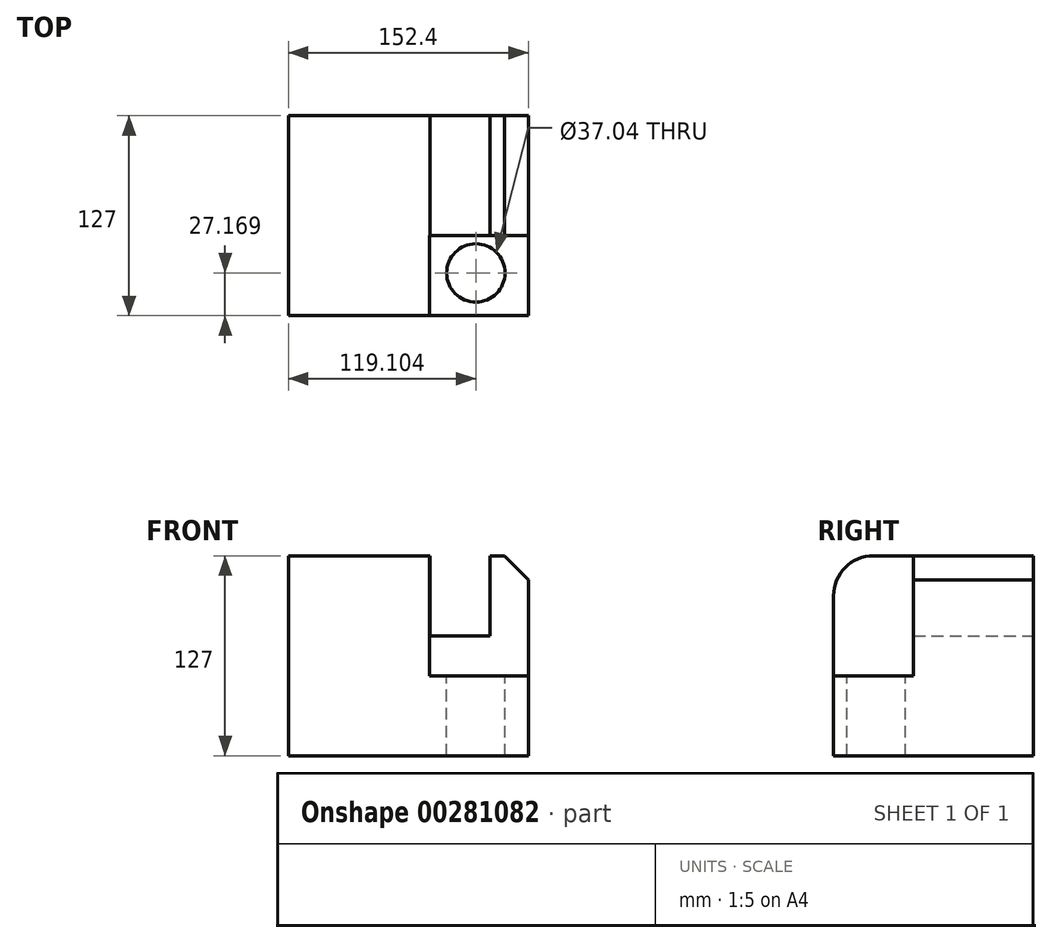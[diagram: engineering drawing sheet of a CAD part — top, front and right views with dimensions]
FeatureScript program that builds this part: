
annotation { "Feature Type Name" : "Feature", "Feature Type Description" : "" }
export const myFeature = defineFeature(function(context is Context, id is Id, definition is map)
    precondition{}
    {
        {
            var Q0;
            Q0=qCreatedBy(makeId("Front.planeOp"),FACE);
            var sketch = newSketch(context, id + "F0", { "sketchPlane" : qUnion([Q0])});
            skLineSegment(sketch, "E0.bottom", {"start": v(-72.36, 54.29) * mm, "end": v(80.04, 54.29) * mm});
            skLineSegment(sketch, "E0.top", {"start": v(-72.36, -72.71) * mm, "end": v(80.04, -72.71) * mm});
            skLineSegment(sketch, "E0.left", {"start": v(-72.36, 54.29) * mm, "end": v(-72.36, -72.71) * mm});
            skLineSegment(sketch, "E0.right", {"start": v(80.04, 54.29) * mm, "end": v(80.04, -72.71) * mm});
            skSolve(sketch);
        }
        {
            var Q0;
            Q0=makeQuery(id+"F0.imprint","IMPRINT",FACE,{"disambiguationData":[TD([[makeQuery(id+"F0.imprint","IMPRINT",EDGE,{"derivedFrom":sQuery(id+"F0.wireOp",EDGE,"E0.bottom")}),-1.0]])]});
            extrude(context, id + "F1", {"entities" : qUnion([Q0]), "depth" : 127 * mm});
        }
        {
            var Q0;
            Q0=makeQuery(id+"F1.opExtrude","SWEPT_FACE",FACE,{"disambiguationData":[OSD([sQuery(id+"F0.wireOp",EDGE,"E0.bottom")])]});
            var sketch = newSketch(context, id + "F2", { "sketchPlane" : qUnion([Q0])});
            skLineSegment(sketch, "E1", {"start": v(80.04, -127) * mm, "end": v(17.28, -127) * mm});
            skLineSegment(sketch, "E2", {"start": v(17.28, -127) * mm, "end": v(17.28, -76.2) * mm});
            skLineSegment(sketch, "E3", {"start": v(17.28, -76.2) * mm, "end": v(80.04, -76.2) * mm});
            skLineSegment(sketch, "E4", {"start": v(80.04, -76.2) * mm, "end": v(80.04, -127) * mm});
            skSolve(sketch);
        }
        {
            var Q0;
            Q0=makeQuery(id+"F2.imprint","IMPRINT",FACE,{"disambiguationData":[TD([[makeQuery(id+"F2.imprint","IMPRINT",EDGE,{"derivedFrom":sQuery(id+"F2.wireOp",EDGE,"E1")}),1.0]])]});
            extrude(context, id + "F3", {"entities" : qUnion([Q0]), "operationType" : NewBodyOperationType.REMOVE, "oppositeDirection" : true, "depth" : 76.2 * mm});
        }
        {
            var Q0;
            Q0=makeQuery(id+"F3.boolean.opBoolean","COPY",FACE,{"derivedFrom":makeQuery(id+"F3.opExtrude","CAP_FACE",FACE,{"disambiguationData":[OSD([sQuery(id+"F2.wireOp",EDGE,"E1"),sQuery(id+"F2.wireOp",EDGE,"E2"),sQuery(id+"F2.wireOp",EDGE,"E3"),sQuery(id+"F2.wireOp",EDGE,"E4")])],"isStart":false})});
            var sketch = newSketch(context, id + "F4", { "sketchPlane" : qUnion([Q0])});
            skCircle(sketch, "E5", {"center": v(46.74, -99.83) * mm, "radius": 18.52 * mm});
            skSolve(sketch);
        }
        {
            var Q0;
            Q0=makeQuery(id+"F4.imprint","IMPRINT",FACE,{"disambiguationData":[TD([[makeQuery(id+"F4.imprint","IMPRINT",EDGE,{"derivedFrom":sQuery(id+"F4.wireOp",EDGE,"E5")}),1.0]])]});
            extrude(context, id + "F5", {"entities" : qUnion([Q0]), "operationType" : NewBodyOperationType.REMOVE, "endBound" : BoundingType.THROUGH_ALL, "oppositeDirection" : true, "depth" : 25.4 * mm});
        }
        {
            var Q0;
            Q0=makeQuery(id+"F1.opExtrude","CAP_EDGE",EDGE,{"disambiguationData":[OSD([sQuery(id+"F0.wireOp",EDGE,"E0.bottom")])],"isStart":false});
            fillet(context, id + "F6", {"entities" : qUnion([Q0]), "radius" : 25.4 * mm, "tangentPropagation" : true, "allowEdgeOverflow" : false});
        }
        {
            var Q0;
            Q0=makeQuery(id+"F1.opExtrude","SWEPT_FACE",FACE,{"disambiguationData":[OSD([sQuery(id+"F0.wireOp",EDGE,"E0.bottom")])]});
            var sketch = newSketch(context, id + "F7", { "sketchPlane" : qUnion([Q0])});
            skLineSegment(sketch, "E6.bottom", {"start": v(55.6, -76.2) * mm, "end": v(17.5, -76.2) * mm});
            skLineSegment(sketch, "E6.top", {"start": v(55.6, 0) * mm, "end": v(17.5, 0) * mm});
            skLineSegment(sketch, "E6.left", {"start": v(55.6, -76.2) * mm, "end": v(55.6, 0) * mm});
            skLineSegment(sketch, "E6.right", {"start": v(17.5, -76.2) * mm, "end": v(17.5, 0) * mm});
            skPoint(sketch, "E6.middle", {"position": v(36.55, -38.1) * mm});
            skSolve(sketch);
        }
        {
            var Q0;
            Q0=makeQuery(id+"F1.opExtrude","SWEPT_EDGE",EDGE,{"disambiguationData":[OSD([sQuery(id+"F0.wireOp",EDGE,"E0.bottom"),sQuery(id+"F0.wireOp",EDGE,"E0.right")])]});
            chamfer(context, id + "F8", {"entities" : qUnion([Q0]), "width" : 15.24 * mm, "tangentPropagation" : true});
        }
        {
            var Q0;
            {var subQ0=sQuery(id+"F7.wireOp",EDGE,"E6.top");Q0=makeQuery(id+"F7.imprint","IMPRINT",FACE,{"disambiguationData":[TD([[makeQuery(id+"F7.imprint","IMPRINT",EDGE,{"derivedFrom":subQ0}),1.0]])]});}
            extrude(context, id + "F9", {"entities" : qUnion([Q0]), "operationType" : NewBodyOperationType.REMOVE, "oppositeDirection" : true, "depth" : 50.8 * mm});
        }
    });
